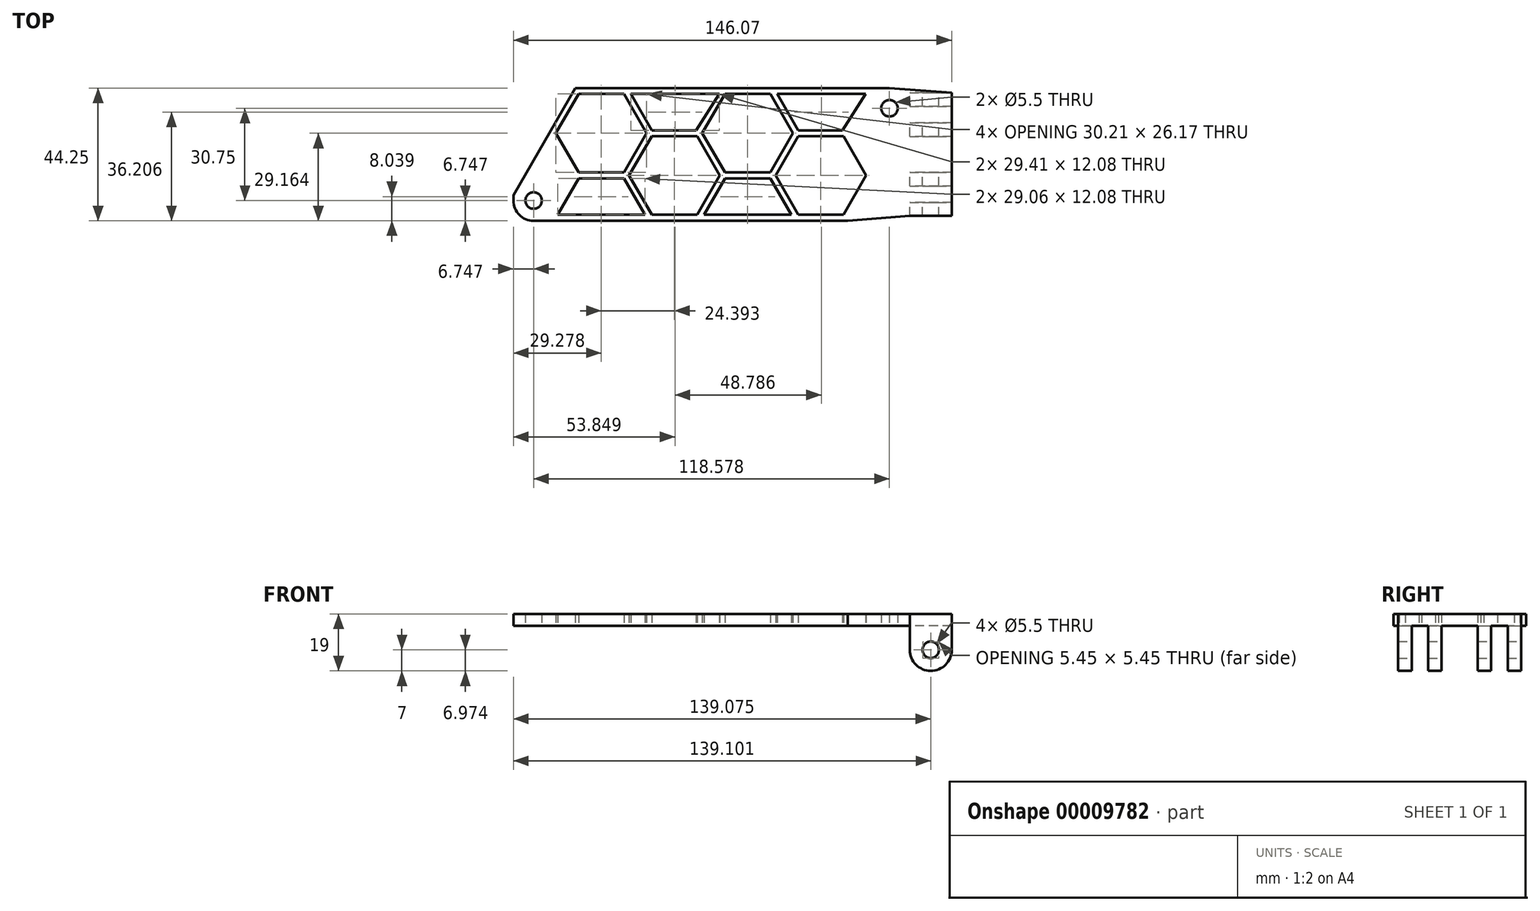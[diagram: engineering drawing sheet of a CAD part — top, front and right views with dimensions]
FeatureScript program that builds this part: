
annotation { "Feature Type Name" : "Feature", "Feature Type Description" : "" }
export const myFeature = defineFeature(function(context is Context, id is Id, definition is map)
    precondition{}
    {
        {
            var Q0;
            Q0=qCreatedBy(makeId("Top.planeOp"),FACE);
            var sketch = newSketch(context, id + "F0", { "sketchPlane" : qUnion([Q0])});
            skLineSegment(sketch, "E0.rect.top", {"start": v(53.83, 3.83) * mm, "end": v(-50.89, 3.83) * mm});
            skLineSegment(sketch, "E0.rect.right", {"start": v(-71.5, -33.67) * mm, "end": v(-71.5, -31.86) * mm});
            skCircle(sketch, "E1", {"center": v(-64.74, -33.67) * mm, "radius": 2.75 * mm});
            skCircle(sketch, "E2", {"center": v(53.83, -2.92) * mm, "radius": 2.75 * mm});
            skLineSegment(sketch, "E3", {"start": v(-50.89, 3.83) * mm, "end": v(-71.5, -31.86) * mm});
            skLineSegment(sketch, "E4", {"start": v(39.98, -40.42) * mm, "end": v(-64.74, -40.42) * mm});
            skLineSegment(sketch, "E5", {"start": v(60.58, -4.73) * mm, "end": v(60.58, -2.92) * mm});
            skLineSegment(sketch, "E6", {"start": v(39.98, -40.42) * mm, "end": v(60.58, -4.73) * mm});
            skArc(sketch, "E7", {"start": v(-71.5, -33.67) * mm, "mid": v(-69.52, -38.45) * mm, "end": v(-64.74, -40.42) * mm});
            skLineSegment(sketch, "E8.1", {"start": v(38.52, -38.42) * mm, "end": v(23.41, -38.42) * mm});
            skPoint(sketch, "E9.0.midPoint", {"position": v(-30.88, -45.96) * mm});
            skPoint(sketch, "E10.0.midPoint", {"position": v(-30.88, -17.8) * mm});
            skLineSegment(sketch, "E11.4", {"start": v(-0.98, 1.83) * mm, "end": v(14.13, 1.83) * mm});
            skLineSegment(sketch, "E12.5", {"start": v(-10.26, -12.26) * mm, "end": v(-2.71, -25.34) * mm});
            skPoint(sketch, "E13.0.midPoint", {"position": v(-6.8, -4.21) * mm});
            skPoint(sketch, "E11.0.midPoint", {"position": v(17.9, -17.8) * mm});
            skCircle(sketch, "E14.cCircle", {"center": v(30.97, 2.83) * mm, "radius": 13.08 * mm, "construction": true});
            skLineSegment(sketch, "E12.4", {"start": v(-25.37, -12.26) * mm, "end": v(-10.26, -12.26) * mm});
            skLineSegment(sketch, "E8.5", {"start": v(38.52, -12.26) * mm, "end": v(46.07, -25.34) * mm});
            skLineSegment(sketch, "E9.3", {"start": v(-56.74, -38.42) * mm, "end": v(-49.77, -26.34) * mm});
            skLineSegment(sketch, "E11.1", {"start": v(14.13, -24.34) * mm, "end": v(-0.98, -24.34) * mm});
            skLineSegment(sketch, "E11.2", {"start": v(-0.98, -24.34) * mm, "end": v(-8.53, -11.26) * mm});
            skLineSegment(sketch, "E10.1", {"start": v(-34.66, -24.34) * mm, "end": v(-49.77, -24.34) * mm});
            skCircle(sketch, "E9.cCircle", {"center": v(-42.21, -39.42) * mm, "radius": 13.08 * mm, "construction": true});
            skLineSegment(sketch, "E15", {"start": v(16.44, 1.83) * mm, "end": v(45.85, 1.83) * mm});
            skCircle(sketch, "E16.cCircle", {"center": v(6.57, -39.42) * mm, "radius": 13.08 * mm, "construction": true});
            skLineSegment(sketch, "E17", {"start": v(21.1, -38.42) * mm, "end": v(-7.96, -38.42) * mm});
            skLineSegment(sketch, "E11.5", {"start": v(14.13, 1.83) * mm, "end": v(21.68, -11.26) * mm});
            skLineSegment(sketch, "E13.2", {"start": v(-25.37, -10.26) * mm, "end": v(-32.35, 1.83) * mm});
            skLineSegment(sketch, "E12.2", {"start": v(-25.37, -38.42) * mm, "end": v(-32.93, -25.34) * mm});
            skCircle(sketch, "E13.cCircle", {"center": v(-17.82, 2.83) * mm, "radius": 13.08 * mm, "construction": true});
            skLineSegment(sketch, "E18", {"start": v(-27.68, -38.42) * mm, "end": v(-56.74, -38.42) * mm});
            skLineSegment(sketch, "E10.4", {"start": v(-49.77, 1.83) * mm, "end": v(-34.66, 1.83) * mm});
            skPoint(sketch, "E8.0.midPoint", {"position": v(42.3, -31.88) * mm});
            skLineSegment(sketch, "E16.4", {"start": v(-0.98, -26.34) * mm, "end": v(14.13, -26.34) * mm});
            skLineSegment(sketch, "E19", {"start": v(-32.35, 1.83) * mm, "end": v(-2.93, 1.83) * mm});
            skLineSegment(sketch, "E10.2", {"start": v(-49.77, -24.34) * mm, "end": v(-57.32, -11.26) * mm});
            skLineSegment(sketch, "E8.4", {"start": v(23.41, -12.26) * mm, "end": v(38.52, -12.26) * mm});
            skLineSegment(sketch, "E10.5", {"start": v(-34.66, 1.83) * mm, "end": v(-27.1, -11.26) * mm});
            skPoint(sketch, "E14.0.midPoint", {"position": v(42, -4.21) * mm});
            skPoint(sketch, "E16.0.midPoint", {"position": v(17.9, -45.96) * mm});
            skLineSegment(sketch, "E10.3", {"start": v(-57.32, -11.26) * mm, "end": v(-49.77, 1.83) * mm});
            skPoint(sketch, "E12.0.midPoint", {"position": v(-6.49, -31.88) * mm});
            skLineSegment(sketch, "E14.1", {"start": v(38.14, -10.26) * mm, "end": v(23.41, -10.26) * mm});
            skLineSegment(sketch, "E9.4", {"start": v(-49.77, -26.34) * mm, "end": v(-34.66, -26.34) * mm});
            skLineSegment(sketch, "E8.2", {"start": v(23.41, -38.42) * mm, "end": v(15.86, -25.34) * mm});
            skLineSegment(sketch, "E16.5", {"start": v(14.13, -26.34) * mm, "end": v(21.1, -38.42) * mm});
            skLineSegment(sketch, "E9.5", {"start": v(-34.66, -26.34) * mm, "end": v(-27.68, -38.42) * mm});
            skLineSegment(sketch, "E13.1", {"start": v(-10.65, -10.26) * mm, "end": v(-25.37, -10.26) * mm});
            skLineSegment(sketch, "E14.2", {"start": v(23.41, -10.26) * mm, "end": v(16.44, 1.83) * mm});
            skLineSegment(sketch, "E12.1", {"start": v(-10.26, -38.42) * mm, "end": v(-25.37, -38.42) * mm});
            skLineSegment(sketch, "E11.0", {"start": v(21.68, -11.26) * mm, "end": v(14.13, -24.34) * mm});
            skLineSegment(sketch, "E14.0", {"start": v(45.85, 1.83) * mm, "end": v(38.14, -10.26) * mm});
            skLineSegment(sketch, "E12.3", {"start": v(-32.93, -25.34) * mm, "end": v(-25.37, -12.26) * mm});
            skLineSegment(sketch, "E10.0", {"start": v(-27.1, -11.26) * mm, "end": v(-34.66, -24.34) * mm});
            skLineSegment(sketch, "E8.0", {"start": v(46.07, -25.34) * mm, "end": v(38.52, -38.42) * mm});
            skCircle(sketch, "E8.cCircle", {"center": v(30.97, -25.34) * mm, "radius": 13.08 * mm, "construction": true});
            skLineSegment(sketch, "E11.3", {"start": v(-8.53, -11.26) * mm, "end": v(-0.98, 1.83) * mm});
            skCircle(sketch, "E12.cCircle", {"center": v(-17.82, -25.34) * mm, "radius": 13.08 * mm, "construction": true});
            skLineSegment(sketch, "E12.0", {"start": v(-2.71, -25.34) * mm, "end": v(-10.26, -38.42) * mm});
            skCircle(sketch, "E11.cCircle", {"center": v(6.57, -11.26) * mm, "radius": 13.08 * mm, "construction": true});
            skLineSegment(sketch, "E8.3", {"start": v(15.86, -25.34) * mm, "end": v(23.41, -12.26) * mm});
            skCircle(sketch, "E10.cCircle", {"center": v(-42.21, -11.26) * mm, "radius": 13.08 * mm, "construction": true});
            skLineSegment(sketch, "E16.3", {"start": v(-7.96, -38.42) * mm, "end": v(-0.98, -26.34) * mm});
            skLineSegment(sketch, "E13.0", {"start": v(-2.93, 1.83) * mm, "end": v(-10.65, -10.26) * mm});
            skLineSegment(sketch, "E20", {"start": v(53.83, 3.83) * mm, "end": v(60.58, -2.92) * mm});
            skSolve(sketch);
        }
        {
            var Q0;
            Q0=makeQuery(id+"F0.imprint","IMPRINT",FACE,{"disambiguationData":[TD([[makeQuery(id+"F0.imprint","IMPRINT",EDGE,{"derivedFrom":sQuery(id+"F0.wireOp",EDGE,"E0.rect.top")}),1.0]])]});
            extrude(context, id + "F1", {"entities" : qUnion([Q0]), "depth" : 4 * mm});
        }
        {
            var Q0;
            Q0=qCreatedBy(makeId("Top.planeOp"),FACE);
            var sketch = newSketch(context, id + "F2", { "sketchPlane" : qUnion([Q0])});
            skLineSegment(sketch, "E21.bottom", {"start": v(60.58, 2.2) * mm, "end": v(74.58, 2.2) * mm});
            skLineSegment(sketch, "E21.top", {"start": v(60.58, -2.3) * mm, "end": v(74.58, -2.3) * mm});
            skLineSegment(sketch, "E21.left", {"start": v(60.58, 2.2) * mm, "end": v(60.58, -2.3) * mm});
            skLineSegment(sketch, "E21.right", {"start": v(74.58, 2.2) * mm, "end": v(74.58, -2.3) * mm});
            skLineSegment(sketch, "E22.bottom", {"start": v(60.58, -7.8) * mm, "end": v(74.58, -7.8) * mm});
            skLineSegment(sketch, "E22.top", {"start": v(60.58, -12.3) * mm, "end": v(74.58, -12.3) * mm});
            skLineSegment(sketch, "E22.left", {"start": v(60.58, -7.8) * mm, "end": v(60.58, -12.3) * mm});
            skLineSegment(sketch, "E22.right", {"start": v(74.58, -7.8) * mm, "end": v(74.58, -12.3) * mm});
            skLineSegment(sketch, "E23.bottom", {"start": v(60.58, -24.3) * mm, "end": v(74.58, -24.3) * mm});
            skLineSegment(sketch, "E23.top", {"start": v(60.58, -28.8) * mm, "end": v(74.58, -28.8) * mm});
            skLineSegment(sketch, "E23.left", {"start": v(60.58, -24.3) * mm, "end": v(60.58, -28.8) * mm});
            skLineSegment(sketch, "E23.right", {"start": v(74.58, -24.3) * mm, "end": v(74.58, -28.8) * mm});
            skLineSegment(sketch, "E24.bottom", {"start": v(60.58, -34.3) * mm, "end": v(74.58, -34.3) * mm});
            skLineSegment(sketch, "E24.top", {"start": v(60.58, -38.8) * mm, "end": v(74.58, -38.8) * mm});
            skLineSegment(sketch, "E24.left", {"start": v(60.58, -34.3) * mm, "end": v(60.58, -38.8) * mm});
            skLineSegment(sketch, "E24.right", {"start": v(74.58, -34.3) * mm, "end": v(74.58, -38.8) * mm});
            skLineSegment(sketch, "E25", {"start": v(74.58, -34.3) * mm, "end": v(74.58, -28.8) * mm, "construction": true});
            skLineSegment(sketch, "E26", {"start": v(74.58, -7.8) * mm, "end": v(74.58, -2.3) * mm, "construction": true});
            skLineSegment(sketch, "E27", {"start": v(74.58, -38.8) * mm, "end": v(74.58, -44.3) * mm, "construction": true});
            skLineSegment(sketch, "E28", {"start": v(74.58, 2.2) * mm, "end": v(74.58, 7.7) * mm, "construction": true});
            skLineSegment(sketch, "E29", {"start": v(38.2, -44.3) * mm, "end": v(38.2, -40.42) * mm, "construction": true});
            skLineSegment(sketch, "E30", {"start": v(51.03, 3.83) * mm, "end": v(51.03, 7.7) * mm, "construction": true});
            skSolve(sketch);
        }
        {
            var Q0;
            Q0=makeQuery(id+"F2.imprint","IMPRINT",FACE,{"disambiguationData":[TD([[makeQuery(id+"F2.imprint","IMPRINT",EDGE,{"derivedFrom":sQuery(id+"F2.wireOp",EDGE,"E21.bottom")}),-1.0]])]});
            var Q1;
            Q1=makeQuery(id+"F2.imprint","IMPRINT",FACE,{"disambiguationData":[TD([[makeQuery(id+"F2.imprint","IMPRINT",EDGE,{"derivedFrom":sQuery(id+"F2.wireOp",EDGE,"E22.bottom")}),-1.0]])]});
            var Q2;
            Q2=makeQuery(id+"F2.imprint","IMPRINT",FACE,{"disambiguationData":[TD([[makeQuery(id+"F2.imprint","IMPRINT",EDGE,{"derivedFrom":sQuery(id+"F2.wireOp",EDGE,"E23.bottom")}),-1.0]])]});
            var Q3;
            Q3=makeQuery(id+"F2.imprint","IMPRINT",FACE,{"disambiguationData":[TD([[makeQuery(id+"F2.imprint","IMPRINT",EDGE,{"derivedFrom":sQuery(id+"F2.wireOp",EDGE,"E24.bottom")}),-1.0]])]});
            extrude(context, id + "F3", {"entities" : qUnion([Q0, Q1, Q2, Q3]), "operationType" : NewBodyOperationType.ADD, "oppositeDirection" : true, "depth" : (6 + 4 * 2 + 1) * mm, "hasSecondDirection" : true, "secondDirectionOppositeDirection" : false, "secondDirectionDepth" : 4 * mm});
        }
        {
            var Q0;
            Q0=makeQuery(id+"F3.opExtrude","CAP_EDGE",EDGE,{"disambiguationData":[OSD([sQuery(id+"F2.wireOp",EDGE,"E21.right")])],"isStart":false});
            var Q1;
            Q1=makeQuery(id+"F3.opExtrude","CAP_EDGE",EDGE,{"disambiguationData":[OSD([sQuery(id+"F2.wireOp",EDGE,"E21.left")])],"isStart":false});
            var Q2;
            Q2=makeQuery(id+"F3.opExtrude","CAP_EDGE",EDGE,{"disambiguationData":[OSD([sQuery(id+"F2.wireOp",EDGE,"E22.left")])],"isStart":false});
            var Q3;
            Q3=makeQuery(id+"F3.opExtrude","CAP_EDGE",EDGE,{"disambiguationData":[OSD([sQuery(id+"F2.wireOp",EDGE,"E22.right")])],"isStart":false});
            var Q4;
            Q4=makeQuery(id+"F3.opExtrude","CAP_EDGE",EDGE,{"disambiguationData":[OSD([sQuery(id+"F2.wireOp",EDGE,"E23.right")])],"isStart":false});
            var Q5;
            Q5=makeQuery(id+"F3.opExtrude","CAP_EDGE",EDGE,{"disambiguationData":[OSD([sQuery(id+"F2.wireOp",EDGE,"E23.left")])],"isStart":false});
            var Q6;
            Q6=makeQuery(id+"F3.opExtrude","CAP_EDGE",EDGE,{"disambiguationData":[OSD([sQuery(id+"F2.wireOp",EDGE,"E24.left")])],"isStart":false});
            var Q7;
            Q7=makeQuery(id+"F3.opExtrude","CAP_EDGE",EDGE,{"disambiguationData":[OSD([sQuery(id+"F2.wireOp",EDGE,"E24.right")])],"isStart":false});
            fillet(context, id + "F4", {"entities" : qUnion([Q0, Q1, Q2, Q3, Q4, Q5, Q6, Q7]), "radius" : 7 * mm, "tangentPropagation" : true, "allowEdgeOverflow" : false});
        }
        {
            var Q0;
            Q0=makeQuery(id+"F3.opExtrude","SWEPT_FACE",FACE,{"disambiguationData":[OSD([sQuery(id+"F2.wireOp",EDGE,"E21.bottom")])]});
            var sketch = newSketch(context, id + "F5", { "sketchPlane" : qUnion([Q0])});
            skLineSegment(sketch, "E31", {"start": v(-60.58, -8) * mm, "end": v(-67.58, -8) * mm});
            skLineSegment(sketch, "E32", {"start": v(-67.58, -8) * mm, "end": v(-67.58, -1) * mm});
            skLineSegment(sketch, "E33", {"start": v(-67.58, -8) * mm, "end": v(-74.58, -8) * mm});
            skCircle(sketch, "E34", {"center": v(-67.58, -8) * mm, "radius": 2.75 * mm});
            skSolve(sketch);
        }
        {
            var Q0;
            Q0 = qSketchRegion(id + "F5", true);
            extrude(context, id + "F6", {"entities" : qUnion([Q0]), "operationType" : NewBodyOperationType.REMOVE, "endBound" : BoundingType.THROUGH_ALL, "oppositeDirection" : true, "depth" : 25 * mm, "hasSecondDirection" : true, "secondDirectionBound" : SecondDirectionBoundingType.THROUGH_ALL, "secondDirectionOppositeDirection" : false, "secondDirectionDepth" : 25 * mm});
        }
        {
            var Q0;
            Q0=qCreatedBy(makeId("Top.planeOp"),FACE);
            var sketch = newSketch(context, id + "F7", { "sketchPlane" : qUnion([Q0])});
            skLineSegment(sketch, "E35.bottom", {"start": v(74.58, -38.8) * mm, "end": v(60.58, -38.8) * mm});
            skLineSegment(sketch, "E35.top", {"start": v(74.58, 2.2) * mm, "end": v(53.83, 3.83) * mm});
            skLineSegment(sketch, "E35.left", {"start": v(74.58, -38.8) * mm, "end": v(74.58, 2.2) * mm});
            skLineSegment(sketch, "E35.right", {"start": v(39.98, -40.42) * mm, "end": v(60.58, -4.73) * mm});
            skLineSegment(sketch, "E36", {"start": v(60.58, -38.8) * mm, "end": v(39.98, -40.42) * mm});
            skLineSegment(sketch, "E37", {"start": v(60.58, -4.73) * mm, "end": v(53.83, 3.83) * mm});
            skSolve(sketch);
        }
        {
            var Q0;
            Q0=makeQuery(id+"F7.imprint","IMPRINT",FACE,{"disambiguationData":[TD([[makeQuery(id+"F7.imprint","IMPRINT",EDGE,{"derivedFrom":sQuery(id+"F7.wireOp",EDGE,"E35.bottom")}),-1.0]])]});
            extrude(context, id + "F8", {"entities" : qUnion([Q0]), "operationType" : NewBodyOperationType.ADD, "depth" : 4 * mm});
        }
    });
